# Revit family: EKF_EE_ПластронГлухойTrivia_AVERES
name_source: partatom
category: Электрооборудование
units: mm (PartAtom-declared; Revit-internal decimal feet)

## family parameters
Всегда вертикально = Нет
На основе рабочей плоскости = Да
Общий = Да
При загрузке вырезать с полостями = Нет
Размер круглого соединителя = Использовать диаметр
Тип детали = Силовой щит
Точка расчета площади = Нет

## types (43) — shared parameters
ADSK_Единица измерения = шт.
ADSK_Завод-изготовитель = EKF
ADSK_Количество = 1
ADSK_Материал = RAL 7035_Сталь
ADSK_Размер_Глубина = 14 мм
Глубина = 400 мм
Изготовитель = EKF
Серия номенклатуры = Averes
Степень защиты IP = -
ТВ = EKF_2_TRIVIA_AVERES
Тип установки = -
Шаг_НабораПластронов_2шт = 100 мм
zero-valued in all types: ADSK_Масса, Отметка по умолчанию

## per-type parameters (varying)
| type | ADSK_Код изделия | ADSK_Марка | ADSK_Наименование | ADSK_Обозначение | ADSK_Размер_Высота | ADSK_Размер_Ширина | Тип | Тип_Пластрона |
| Пластрон В55 Ш800 (2шт) EKF AVERES | FP5M800B | Пластрон В55 Ш800 (2 шт) EKF AVERES | Пластрон В55 Ш800 (2 шт) EKF AVERES | Пластрон В55 Ш800 (2 шт) EKF AVERES | 55 мм | 690 мм | 600 мм | Вл_Пластрон4 |
| Пластрон В55 Ш600 (2шт) EKF AVERES | FP5M600B | Пластрон В55 Ш600 (2 шт) EKF AVERES | Пластрон В55 Ш600 (2 шт) EKF AVERES | Пластрон В55 Ш600 (2 шт) EKF AVERES | 55 мм | 490 мм | 599 мм | Вл_Пластрон4 |
| Пластрон В55 Ш400 (2шт) EKF AVERES | FP5M400B | Пластрон В55 Ш400 (2 шт) EKF AVERES | Пластрон В55 Ш400 (2 шт) EKF AVERES | Пластрон В55 Ш400 (2 шт) EKF AVERES | 55 мм | 290 мм | 598 мм | Вл_Пластрон4 |
| Пластрон В50 Ш800 EKF AVERES | FP5M800 | Пластрон В50 Ш800 EKF AVERES | Пластрон В50 Ш800 EKF AVERES | Пластрон В50 Ш800 EKF AVERES | 50 мм | 690 мм | 594 мм | Вл_Пластрон3 |
| Пластрон В50 Ш600 EKF AVERES | FP5M600 | Пластрон В50 Ш600 EKF AVERES | Пластрон В50 Ш600 EKF AVERES | Пластрон В50 Ш600 EKF AVERES | 50 мм | 490 мм | 593 мм | Вл_Пластрон3 |
| Пластрон В50 Ш400 EKF AVERES | FP5M400 | Пластрон В50 Ш400 EKF AVERES | Пластрон В50 Ш400 EKF AVERES | Пластрон В50 Ш400 EKF AVERES | 50 мм | 290 мм | 592 мм | Вл_Пластрон3 |
| Пластрон В50 Ш300 EKF AVERES | FP5M300 | Пластрон В50 Ш300 EKF AVERES | Пластрон В50 Ш300 EKF AVERES | Пластрон В50 Ш300 EKF AVERES | 50 мм | 190 мм | 591 мм | Вл_Пластрон3 |
| Пластрон В100 Ш400 EKF AVERES | FP10M400 | Пластрон В100 Ш400 EKF AVERES | Пластрон В100 Ш400 EKF AVERES | Пластрон В100 Ш400 EKF AVERES | 100 мм | 290 мм | 565 мм | Вл_Пластрон3 |
| Пластрон В100 Ш600 EKF AVERES | FP10M600 | Пластрон В100 Ш600 EKF AVERES | Пластрон В100 Ш600 EKF AVERES | Пластрон В100 Ш600 EKF AVERES | 100 мм | 490 мм | 566 мм | Вл_Пластрон3 |
| Пластрон В100 Ш800 EKF AVERES | FP10M800 | Пластрон В100 Ш800 EKF AVERES | Пластрон В100 Ш800 EKF AVERES | Пластрон В100 Ш800 EKF AVERES | 100 мм | 690 мм | 567 мм | Вл_Пластрон3 |
| Пластрон В150 Ш300 EKF AVERES | FP15M300 | Пластрон В150 Ш300 EKF AVERES | Пластрон В150 Ш300 EKF AVERES | Пластрон В150 Ш300 EKF AVERES | 150 мм | 190 мм | 568 мм | Вл_Пластрон3 |
| Пластрон В150 Ш400 EKF AVERES | FP15M400 | Пластрон В150 Ш400 EKF AVERES | Пластрон В150 Ш400 EKF AVERES | Пластрон В150 Ш400 EKF AVERES | 150 мм | 290 мм | 569 мм | Вл_Пластрон3 |
| Пластрон В150 Ш600 EKF AVERES | FP15M600 | Пластрон В150 Ш600 EKF AVERES | Пластрон В150 Ш600 EKF AVERES | Пластрон В150 Ш600 EKF AVERES | 150 мм | 490 мм | 570 мм | Вл_Пластрон3 |
| Пластрон В150 Ш800 EKF AVERES | FP15M800 | Пластрон В150 Ш800 EKF AVERES | Пластрон В150 Ш800 EKF AVERES | Пластрон В150 Ш800 EKF AVERES | 150 мм | 690 мм | 571 мм | Вл_Пластрон3 |
| Пластрон В200 Ш400 EKF AVERES | FP20M400 | Пластрон В200 Ш400 EKF AVERES | Пластрон В200 Ш400 EKF AVERES | Пластрон В200 Ш400 EKF AVERES | 200 мм | 290 мм | 572 мм | Вл_Пластрон3 |
| Пластрон В200 Ш600 EKF AVERES | FP20M600 | Пластрон В200 Ш600 EKF AVERES | Пластрон В200 Ш600 EKF AVERES | Пластрон В200 Ш600 EKF AVERES | 200 мм | 490 мм | 573 мм | Вл_Пластрон3 |
| Пластрон В200 Ш800 EKF AVERES | FP20M800 | Пластрон В200 Ш800 EKF AVERES | Пластрон В200 Ш800 EKF AVERES | Пластрон В200 Ш800 EKF AVERES | 200 мм | 690 мм | 574 мм | Вл_Пластрон3 |
| Пластрон В250 Ш400 EKF AVERES | FP25M400 | Пластрон В250 Ш400 EKF AVERES | Пластрон В250 Ш400 EKF AVERES | Пластрон В250 Ш400 EKF AVERES | 250 мм | 290 мм | 575 мм | Вл_Пластрон3 |
| Пластрон В250 Ш600 EKF AVERES | FP25M600 | Пластрон В250 Ш600 EKF AVERES | Пластрон В250 Ш600 EKF AVERES | Пластрон В250 Ш600 EKF AVERES | 250 мм | 490 мм | 576 мм | Вл_Пластрон3 |
| Пластрон В250 Ш800 EKF AVERES | FP25M800 | Пластрон В250 Ш800 EKF AVERES | Пластрон В250 Ш800 EKF AVERES | Пластрон В250 Ш800 EKF AVERES | 250 мм | 690 мм | 577 мм | Вл_Пластрон3 |
| Пластрон В300 Ш400 EKF AVERES | FP30M400 | Пластрон В300 Ш400 EKF AVERES | Пластрон В300 Ш400 EKF AVERES | Пластрон В300 Ш400 EKF AVERES | 300 мм | 290 мм | 578 мм | Вл_Пластрон3 |
| Пластрон В300 Ш600 EKF AVERES | FP30M600 | Пластрон В300 Ш600 EKF AVERES | Пластрон В300 Ш600 EKF AVERES | Пластрон В300 Ш600 EKF AVERES | 300 мм | 490 мм | 579 мм | Вл_Пластрон3 |
| Пластрон В300 Ш800 EKF AVERES | FP30M800 | Пластрон В300 Ш800 EKF AVERES | Пластрон В300 Ш800 EKF AVERES | Пластрон В300 Ш800 EKF AVERES | 300 мм | 690 мм | 580 мм | Вл_Пластрон3 |
| Пластрон В350 Ш300 EKF AVERES | FP35M300 | Пластрон В350 Ш300 EKF AVERES | Пластрон В350 Ш300 EKF AVERES | Пластрон В350 Ш300 EKF AVERES | 350 мм | 190 мм | 581 мм | Вл_Пластрон3 |
| Пластрон В350 Ш400 EKF AVERES | FP35M400 | Пластрон В350 Ш400 EKF AVERES | Пластрон В350 Ш400 EKF AVERES | Пластрон В350 Ш400 EKF AVERES | 350 мм | 290 мм | 582 мм | Вл_Пластрон3 |
| Пластрон В350 Ш600 EKF AVERES | FP35M600 | Пластрон В350 Ш600 EKF AVERES | Пластрон В350 Ш600 EKF AVERES | Пластрон В350 Ш600 EKF AVERES | 350 мм | 490 мм | 583 мм | Вл_Пластрон3 |
| Пластрон В350 Ш800 EKF AVERES | FP35M800 | Пластрон В350 Ш800 EKF AVERES | Пластрон В350 Ш800 EKF AVERES | Пластрон В350 Ш800 EKF AVERES | 350 мм | 690 мм | 584 мм | Вл_Пластрон3 |
| Пластрон В400 Ш400 EKF AVERES | FP40M400 | Пластрон В400 Ш400 EKF AVERES | Пластрон В400 Ш400 EKF AVERES | Пластрон В400 Ш400 EKF AVERES | 400 мм | 290 мм | 585 мм | Вл_Пластрон3 |
| Пластрон В400 Ш600 EKF AVERES | FP40M600 | Пластрон В400 Ш600 EKF AVERES | Пластрон В400 Ш600 EKF AVERES | Пластрон В400 Ш600 EKF AVERES | 400 мм | 490 мм | 586 мм | Вл_Пластрон3 |
| Пластрон В400 Ш800 EKF AVERES | FP40M800 | Пластрон В400 Ш800 EKF AVERES | Пластрон В400 Ш800 EKF AVERES | Пластрон В400 Ш800 EKF AVERES | 400 мм | 690 мм | 587 мм | Вл_Пластрон3 |
| Пластрон В450 Ш400 EKF AVERES | FP45M400 | Пластрон В450 Ш400 EKF AVERES | Пластрон В450 Ш400 EKF AVERES | Пластрон В450 Ш400 EKF AVERES | 450 мм | 290 мм | 588 мм | Вл_Пластрон3 |
| Пластрон В450 Ш600 EKF AVERES | FP45M600 | Пластрон В450 Ш600 EKF AVERES | Пластрон В450 Ш600 EKF AVERES | Пластрон В450 Ш600 EKF AVERES | 450 мм | 490 мм | 589 мм | Вл_Пластрон3 |
| Пластрон В450 Ш800 EKF AVERES | FP45M800 | Пластрон В450 Ш800 EKF AVERES | Пластрон В450 Ш800 EKF AVERES | Пластрон В450 Ш800 EKF AVERES | 450 мм | 690 мм | 590 мм | Вл_Пластрон3 |
| Пластрон В500 Ш400 EKF AVERES | FP50M400 | Пластрон В500 Ш400 EKF AVERES | Пластрон В500 Ш400 EKF AVERES | Пластрон В500 Ш400 EKF AVERES | 500 мм | 290 мм | 595 мм | Вл_Пластрон3 |
| Пластрон В500 Ш600 EKF AVERES | FP50M600 | Пластрон В500 Ш600 EKF AVERES | Пластрон В500 Ш600 EKF AVERES | Пластрон В500 Ш600 EKF AVERES | 500 мм | 490 мм | 596 мм | Вл_Пластрон3 |
| Пластрон В500 Ш800 EKF AVERES | FP50M800 | Пластрон В500 Ш800 EKF AVERES | Пластрон В500 Ш800 EKF AVERES | Пластрон В500 Ш800 EKF AVERES | 500 мм | 690 мм | 597 мм | Вл_Пластрон3 |
| Пластрон В550 Ш400 EKF AVERES | FP55M400 | Пластрон В550 Ш400 EKF AVERES | Пластрон В550 Ш400 EKF AVERES | Пластрон В550 Ш400 EKF AVERES | 550 мм | 290 мм | 601 мм | Вл_Пластрон3 |
| Пластрон В550 Ш600 EKF AVERES | FP55M600 | Пластрон В550 Ш600 EKF AVERES | Пластрон В550 Ш600 EKF AVERES | Пластрон В550 Ш600 EKF AVERES | 550 мм | 490 мм | 602 мм | Вл_Пластрон3 |
| Пластрон В550 Ш800 EKF AVERES | FP55M800 | Пластрон В550 Ш800 EKF AVERES | Пластрон В550 Ш800 EKF AVERES | Пластрон В550 Ш800 EKF AVERES | 550 мм | 690 мм | 603 мм | Вл_Пластрон3 |
| Пластрон В600 Ш300 EKF AVERES | FP60M300 | Пластрон В600 Ш300 EKF AVERES | Пластрон В600 Ш300 EKF AVERES | Пластрон В600 Ш300 EKF AVERES | 600 мм | 190 мм | 604 мм | Вл_Пластрон3 |
| Пластрон В600 Ш400 EKF AVERES | FP60M400 | Пластрон В600 Ш400 EKF AVERES | Пластрон В600 Ш400 EKF AVERES | Пластрон В600 Ш400 EKF AVERES | 600 мм | 290 мм | 605 мм | Вл_Пластрон3 |
| Пластрон В600 Ш600 EKF AVERES | FP60M600 | Пластрон В600 Ш600 EKF AVERES | Пластрон В600 Ш600 EKF AVERES | Пластрон В600 Ш600 EKF AVERES | 600 мм | 490 мм | 606 мм | Вл_Пластрон3 |
| Пластрон В600 Ш800 EKF AVERES | FP60M800 | Пластрон В600 Ш800 EKF AVERES | Пластрон В600 Ш800 EKF AVERES | Пластрон В600 Ш800 EKF AVERES | 600 мм | 690 мм | 607 мм | Вл_Пластрон3 |
